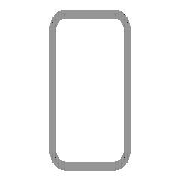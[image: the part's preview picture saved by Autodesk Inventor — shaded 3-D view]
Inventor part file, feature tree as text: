
AUTODESK INVENTOR PART (.ipt)
format: ipt  version: 2025 (Build 290162010, 162A)  size: 133,120 bytes
history: native  units: mm (DEFAULTED — no unit token found)
features: other x4, sketch x1, plane x1
ambient origin geometry x8: Origin, YZ Plane, XZ Plane, XY Plane, X Axis, Y Axis, Z Axis, Center Point
bodies: Solid1 (feature_tree), Body (feature_tree)
feature tree (6):
  parser-record x1  (decoder bookkeeping rows leaked as tree rows — omitted from the tree; the rows remain in map.json)
  other  "Driven Length"
  other  "Start Plane"
  other  "End Plane"
  sketch  "Sketch3"  dims[d3=720.0mm d4=0.0mm d7=6.0mm d9=40.0mm d11=60.0mm d12=3.0mm d13=40.0mm d14=760.0mm d15=20.0mm d16=30.0mm d17=90.0deg d18=720.0mm]
  plane  "Work Plane3"
